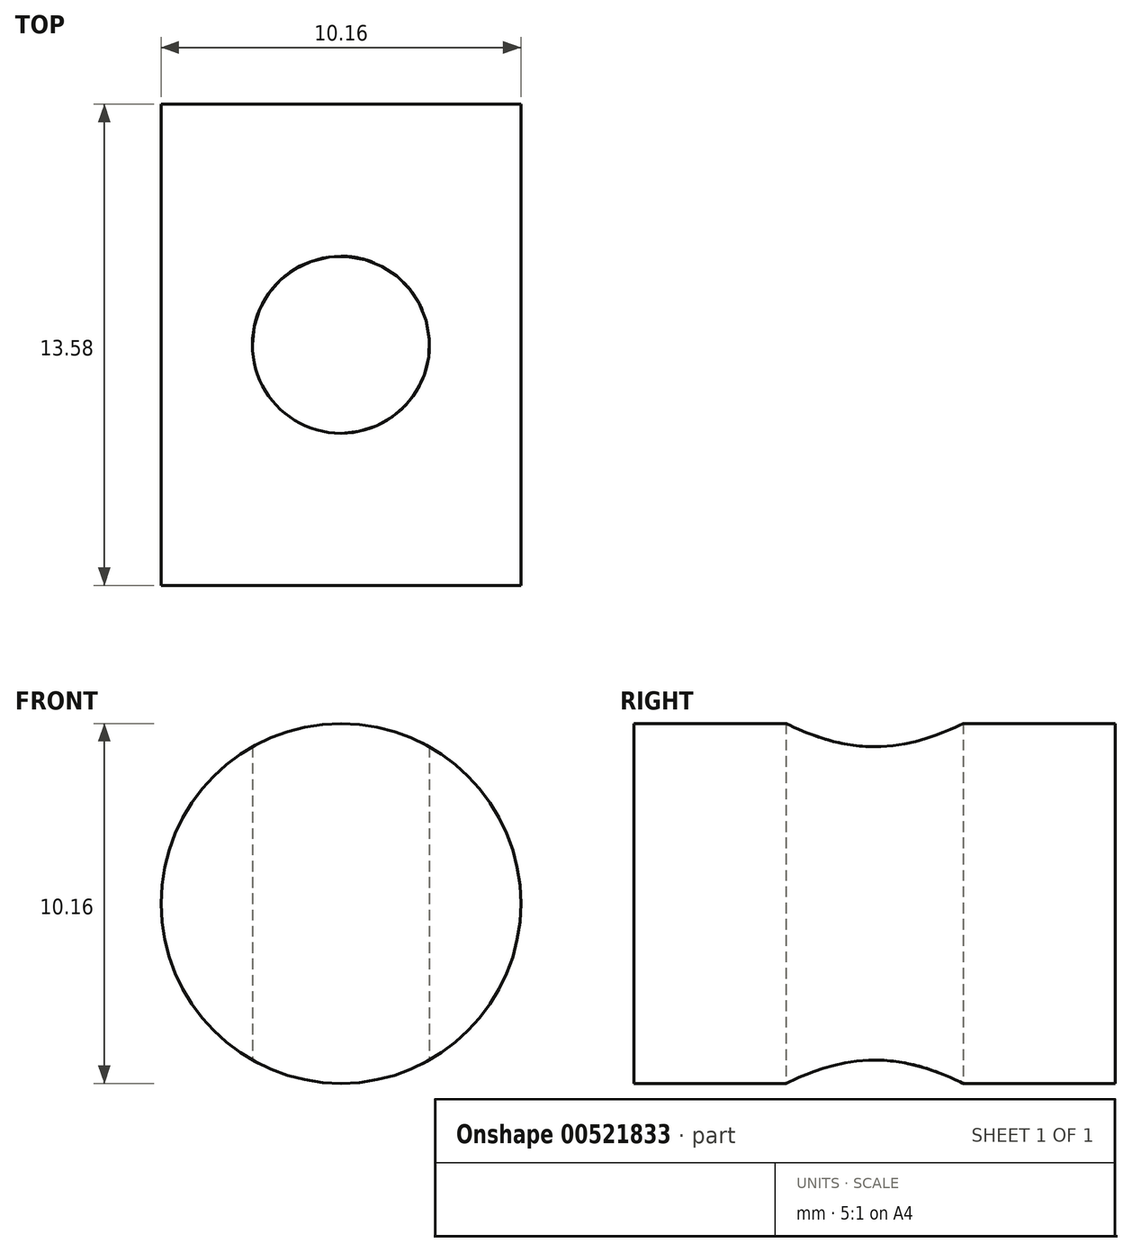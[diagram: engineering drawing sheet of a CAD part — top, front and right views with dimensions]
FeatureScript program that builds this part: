
annotation { "Feature Type Name" : "Feature", "Feature Type Description" : "" }
export const myFeature = defineFeature(function(context is Context, id is Id, definition is map)
    precondition{}
    {
        {
            var Q0;
            Q0=qCreatedBy(makeId("Front.planeOp"),FACE);
            var sketch = newSketch(context, id + "F0", { "sketchPlane" : qUnion([Q0])});
            skCircle(sketch, "E0", {"center": v(0, 0) * mm, "radius": 5.08 * mm});
            skSolve(sketch);
        }
        {
            var Q0;
            Q0 = qSketchRegion(id + "F0", true);
            extrude(context, id + "F1", {"entities" : qUnion([Q0]), "endBound" : BoundingType.SYMMETRIC, "depth" : 13.6 * mm, "offsetDistance" : 25.4 * mm});
        }
        {
            var Q0;
            Q0=qCreatedBy(makeId("Top.planeOp"),FACE);
            cPlane(context, id + "F2", {"entities" : qUnion([Q0]), "cplaneType" : CPlaneType.OFFSET, "offset" : 10.16 * mm, "oppositeDirection" : true, "width" : 152.4 * mm, "height" : 152.4 * mm});
        }
        {
            var Q0;
            Q0=qCreatedBy(id+"F2.planeOp",FACE);
            var sketch = newSketch(context, id + "F3", { "sketchPlane" : qUnion([Q0])});
            skPoint(sketch, "E1", {"position": v(0, 0) * mm});
            skSolve(sketch);
        }
        {
            var Q0;
            Q0=sQuery(id+"F3.wireOp",VERTEX,"E1");
            var Q1;
            Q1=makeQuery(id+"F1.opExtrude","SWEPT_BODY",BODY,{"disambiguationData":[OSD([sQuery(id+"F0.wireOp",EDGE,"E0")])]});
            hole(context, id + "F4", {"style" : HoleStyle.SIMPLE, "endStyle" : HoleEndStyle.THROUGH, "oppositeDirection" : true, "standardTappedOrClearance" : lookupTablePath({ "standard" : "ISO", "engagement" : "75%", "pitch" : "1 mm", "size" : "M6", "type" : "Tapped" }), "standardBlindInLast" : lookupTablePath({ "standard" : "ISO", "engagement" : "75%", "pitch" : "1 mm", "size" : "M6", "type" : "Tapped" }), "holeDiameter" : 5 * mm, "showTappedDepth" : true, "isTappedThrough" : true, "tappedDepth" : 12.7 * mm, "tapClearance" : 3, "locations" : qUnion([Q0]), "scope" : qUnion([Q1]), "majorDiameter" : 6 * mm});
        }
    });
